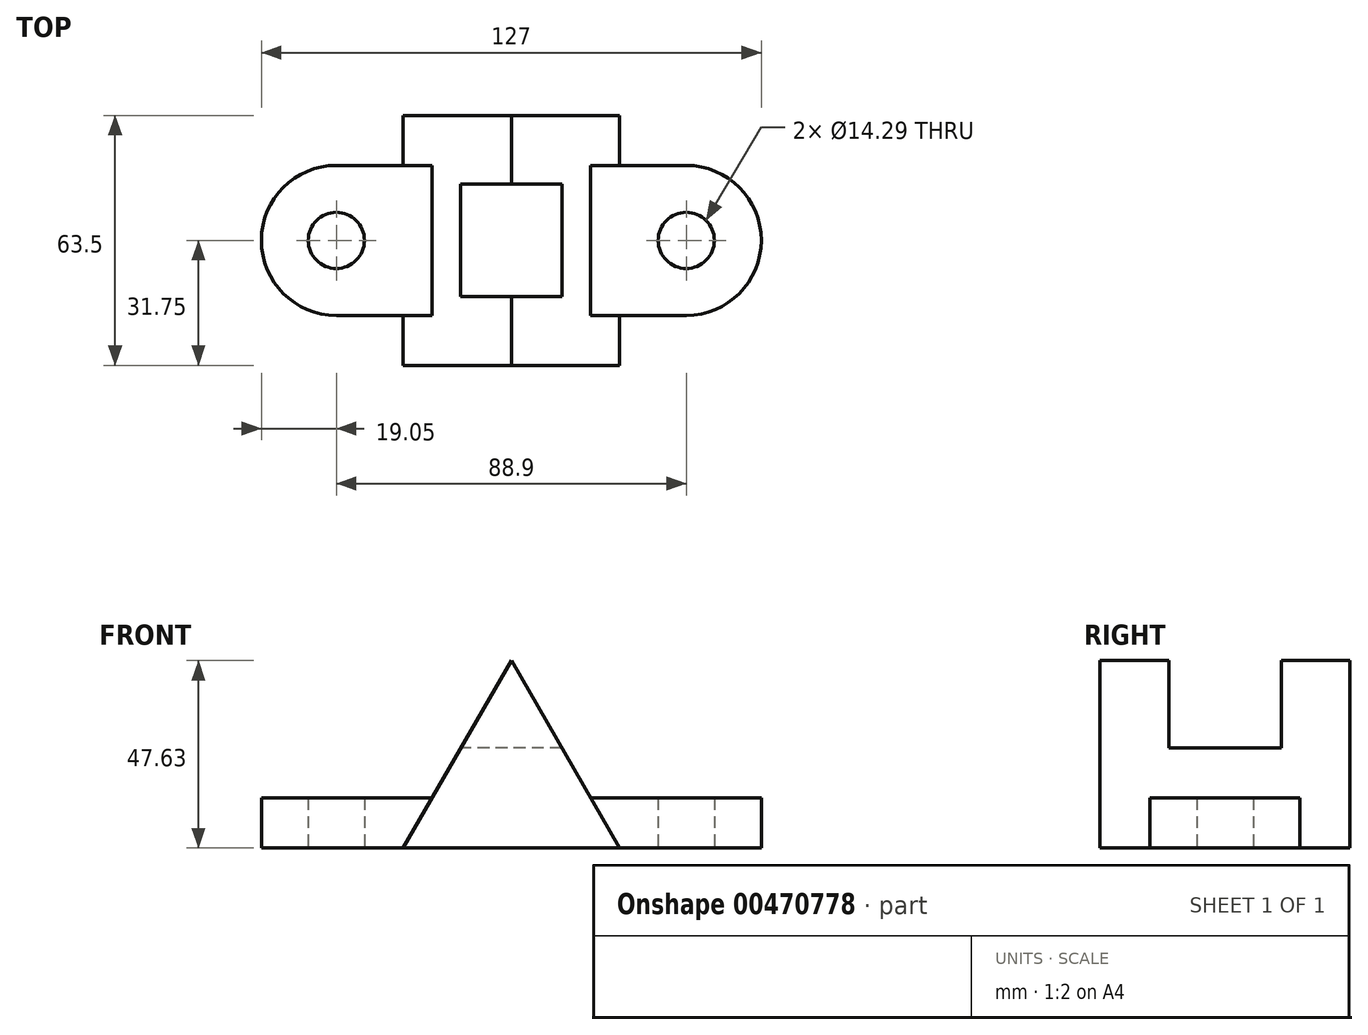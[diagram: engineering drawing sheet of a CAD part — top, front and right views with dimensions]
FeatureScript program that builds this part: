
annotation { "Feature Type Name" : "Feature", "Feature Type Description" : "" }
export const myFeature = defineFeature(function(context is Context, id is Id, definition is map)
    precondition{}
    {
        {
            var Q0;
            Q0=qCreatedBy(makeId("Top.planeOp"),FACE);
            var sketch = newSketch(context, id + "F0", { "sketchPlane" : qUnion([Q0])});
            skArc(sketch, "E0", {"start": v(88.9, -19.05) * mm, "mid": v(107.95, 0) * mm, "end": v(88.9, 19.05) * mm});
            skArc(sketch, "E1", {"start": v(0, 19.05) * mm, "mid": v(-19.05, 0) * mm, "end": v(0, -19.05) * mm});
            skLineSegment(sketch, "E2", {"start": v(0, 19.05) * mm, "end": v(88.9, 19.05) * mm});
            skLineSegment(sketch, "E3", {"start": v(0, -19.05) * mm, "end": v(88.9, -19.05) * mm});
            skCircle(sketch, "E4", {"center": v(0, 0) * mm, "radius": 7.14 * mm});
            skCircle(sketch, "E5", {"center": v(88.9, 0) * mm, "radius": 7.14 * mm});
            skSolve(sketch);
        }
        {
            var Q0;
            Q0 = qSketchRegion(id + "F0", true);
            extrude(context, id + "F1", {"entities" : qUnion([Q0]), "depth" : 12.7 * mm});
        }
        {
            var Q0;
            Q0=qCreatedBy(makeId("Front.planeOp"),FACE);
            var sketch = newSketch(context, id + "F2", { "sketchPlane" : qUnion([Q0])});
            skLineSegment(sketch, "E6", {"start": v(16.95, 0) * mm, "end": v(71.95, 0) * mm});
            skLineSegment(sketch, "E7", {"start": v(0, 0) * mm, "end": v(44.45, 0) * mm});
            skLineSegment(sketch, "E8", {"start": v(44.45, 0) * mm, "end": v(44.45, 47.63) * mm});
            skLineSegment(sketch, "E9", {"start": v(44.45, 47.63) * mm, "end": v(16.95, 0) * mm});
            skLineSegment(sketch, "E10", {"start": v(44.45, 47.62) * mm, "end": v(71.95, 0) * mm});
            skSolve(sketch);
        }
        {
            var Q0;
            Q0 = qSketchRegion(id + "F2", true);
            extrude(context, id + "F3", {"entities" : qUnion([Q0]), "operationType" : NewBodyOperationType.ADD, "endBound" : BoundingType.SYMMETRIC, "depth" : 63.5 * mm});
        }
        {
            var Q0;
            Q0=qCreatedBy(makeId("Right.planeOp"),FACE);
            var sketch = newSketch(context, id + "F4", { "sketchPlane" : qUnion([Q0])});
            skLineSegment(sketch, "E11", {"start": v(0, 25.4) * mm, "end": v(-14.29, 25.4) * mm});
            skLineSegment(sketch, "E12", {"start": v(-14.29, 25.4) * mm, "end": v(14.29, 25.4) * mm});
            skLineSegment(sketch, "E13", {"start": v(14.29, 25.4) * mm, "end": v(14.29, 47.63) * mm});
            skLineSegment(sketch, "E14", {"start": v(14.29, 47.63) * mm, "end": v(-14.29, 47.63) * mm});
            skLineSegment(sketch, "E15", {"start": v(-14.29, 47.63) * mm, "end": v(-14.29, 25.4) * mm});
            skSolve(sketch);
        }
        {
            var Q0;
            Q0 = qSketchRegion(id + "F4", true);
            extrude(context, id + "F5", {"entities" : qUnion([Q0]), "operationType" : NewBodyOperationType.REMOVE, "endBound" : BoundingType.THROUGH_ALL, "depth" : 25.4 * mm});
        }
    });
